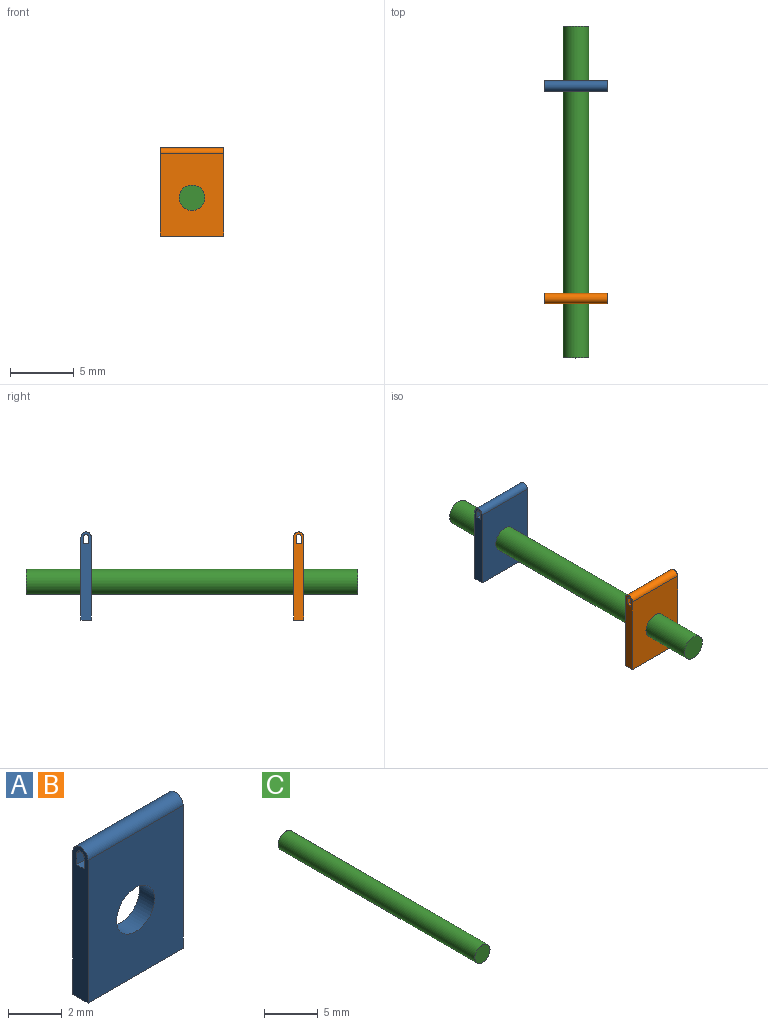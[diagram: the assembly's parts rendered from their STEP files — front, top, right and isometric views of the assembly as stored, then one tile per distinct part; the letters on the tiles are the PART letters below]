
ASSEMBLY  parts=3 mates=2
PART A: 11 faces, bbox 5x0.8x6.9 mm
  f0: cylinder r=0.4mm len=5mm, axis (-1,0,0), area 6.3mm2, adj f1,f7,f8,f9
  f1: plane 6.5x5mm, normal (0,-1,0), area 29.4mm2, adj f0,f2,f8,f9,f10
  f2: plane 5x0.8mm, normal (0,0,-1), area 4mm2, adj f1,f7,f8,f9
  f3: plane 5x0.5mm, normal (0,1,0), area 2.5mm2, adj f4,f6,f8,f9
  f4: cylinder r=0.2mm len=5mm, axis (-1,0,0), area 3.1mm2, adj f3,f5,f8,f9
  f5: plane 5x0.5mm, normal (0,-1,0), area 2.5mm2, adj f4,f6,f8,f9
  f6: plane 5x0.4mm, normal (0,0,1), area 2mm2, adj f3,f5,f8,f9
  f7: plane 6.5x5mm, normal (0,1,0), area 29.4mm2, adj f0,f2,f8,f9,f10
  f8: plane 6.9x0.8mm, normal (1,0,0), area 5.2mm2, adj f0,f1,f2,f3,f4,f5,f6,f7
  f9: plane 6.9x0.8mm, normal (-1,0,0), area 5.2mm2, adj f0,f1,f2,f3,f4,f5,f6,f7
  f10: cylinder r=1mm len=2mm, axis (0,-1,0), area 5mm2, adj f1,f7
PART B: same geometry as A
PART C: 3 faces, bbox 2x26x2 mm
  f0: cylinder r=1mm len=26mm, axis (0,1,0), area 163.4mm2, adj f1,f2
  f1: plane 2x2mm, normal (0,-1,0), area 3.1mm2, adj f0
  f2: plane 2x2mm, normal (0,1,0), area 3.1mm2, adj f0
PLACE A t=(1.97,10.29,0.08)mm
PLACE B t=(1.97,-6.35,0.08)mm
PLACE C t=(-9.71,15,0.08)mm
MATE slider C.f0 <-> B.f10  axis (0,1,0) through (4.47,-11,0.08)mm
MATE slider C.f0 <-> A.f10  axis (0,1,0) through (4.47,2,0.08)mm
